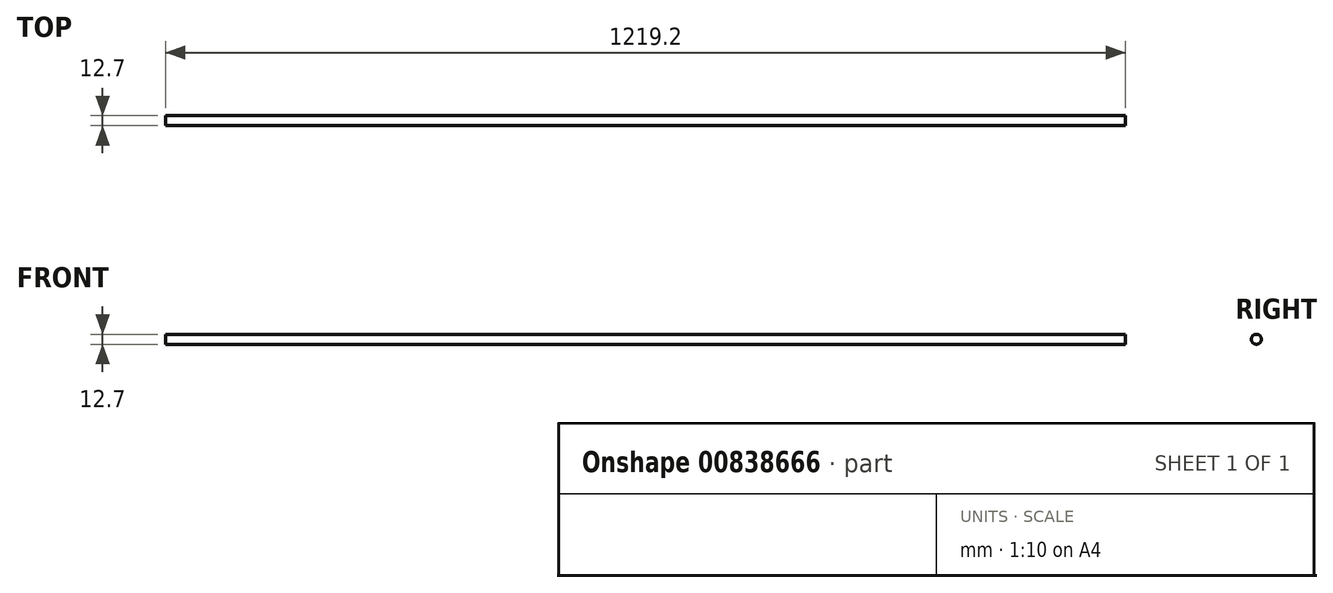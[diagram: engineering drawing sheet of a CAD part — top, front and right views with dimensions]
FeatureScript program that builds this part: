
annotation { "Feature Type Name" : "Feature", "Feature Type Description" : "" }
export const myFeature = defineFeature(function(context is Context, id is Id, definition is map)
    precondition{}
    {
        {
            var Q0;
            Q0=qCreatedBy(makeId("Right.planeOp"),FACE);
            var sketch = newSketch(context, id + "F0", { "sketchPlane" : qUnion([Q0])});
            skCircle(sketch, "E0", {"center": v(0, 0) * mm, "radius": 6.35 * mm});
            skSolve(sketch);
        }
        {
            var Q0;
            Q0=qSketchRegion(id+"F0",true);
            extrude(context, id + "F1", {"entities" : qUnion([Q0]), "depth" : 1219.2 * mm, "offsetDistance" : 25.4 * mm, "symmetric" : true});
        }
    });
